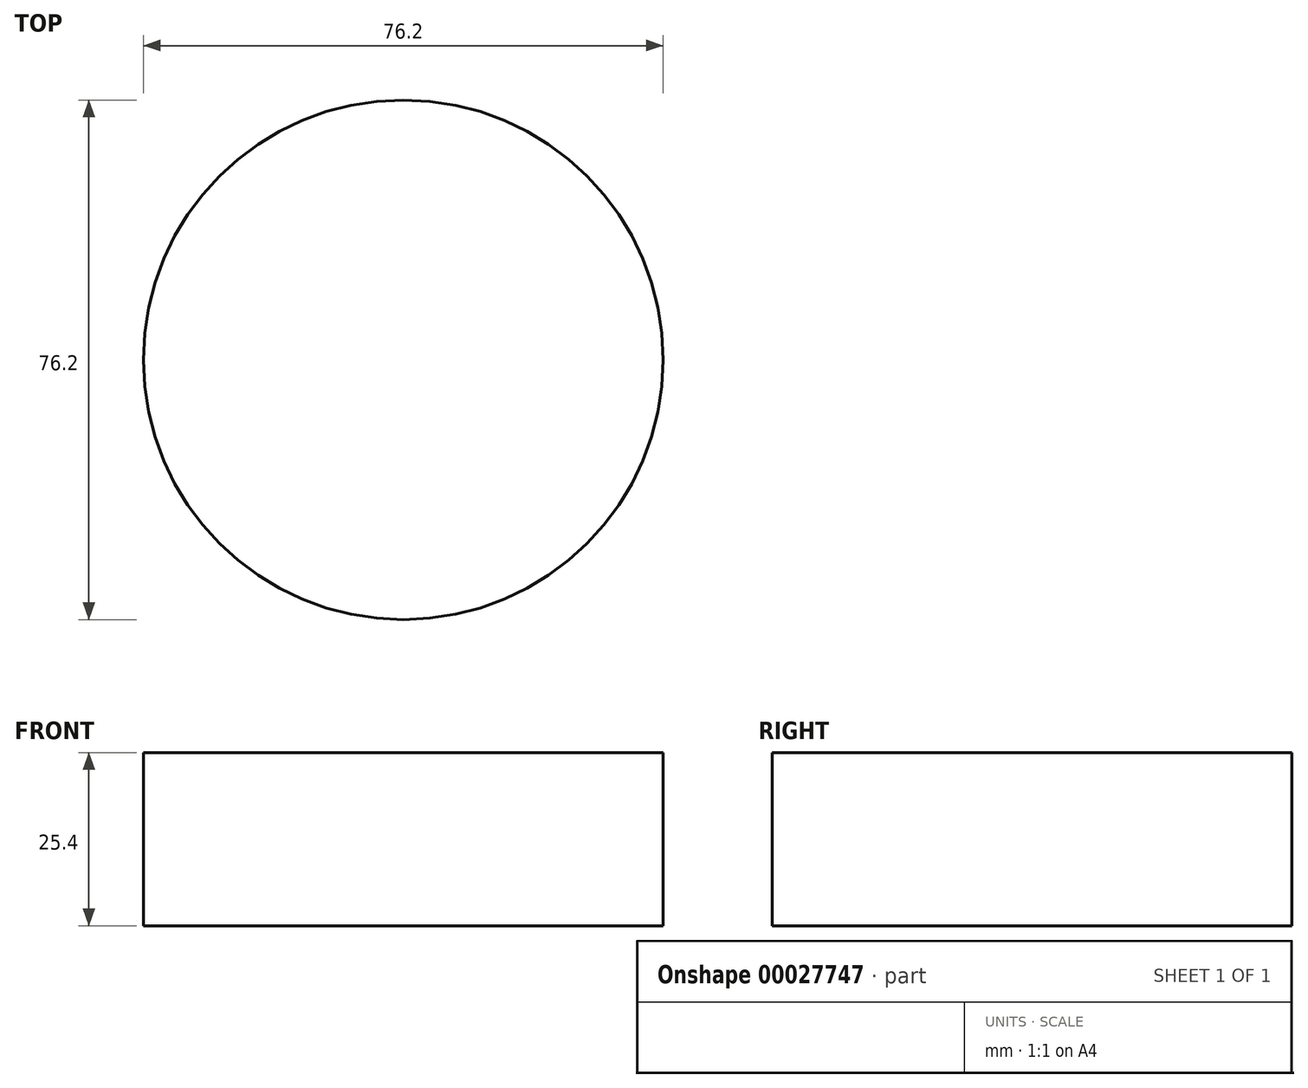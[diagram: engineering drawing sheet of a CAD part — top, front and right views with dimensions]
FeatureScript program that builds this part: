
annotation { "Feature Type Name" : "Feature", "Feature Type Description" : "" }
export const myFeature = defineFeature(function(context is Context, id is Id, definition is map)
    precondition{}
    {
        {
            var Q0;
            Q0=qCreatedBy(makeId("Top.planeOp"),FACE);
            var sketch = newSketch(context, id + "F0", { "sketchPlane" : qUnion([Q0])});
            skCircle(sketch, "E0", {"center": v(0, 0) * mm, "radius": 38.1 * mm});
            skSolve(sketch);
        }
        {
            var Q0;
            Q0 = qSketchRegion(id + "F0", true);
            extrude(context, id + "F1", {"entities" : qUnion([Q0]), "depth" : 25.4 * mm});
        }
    });
